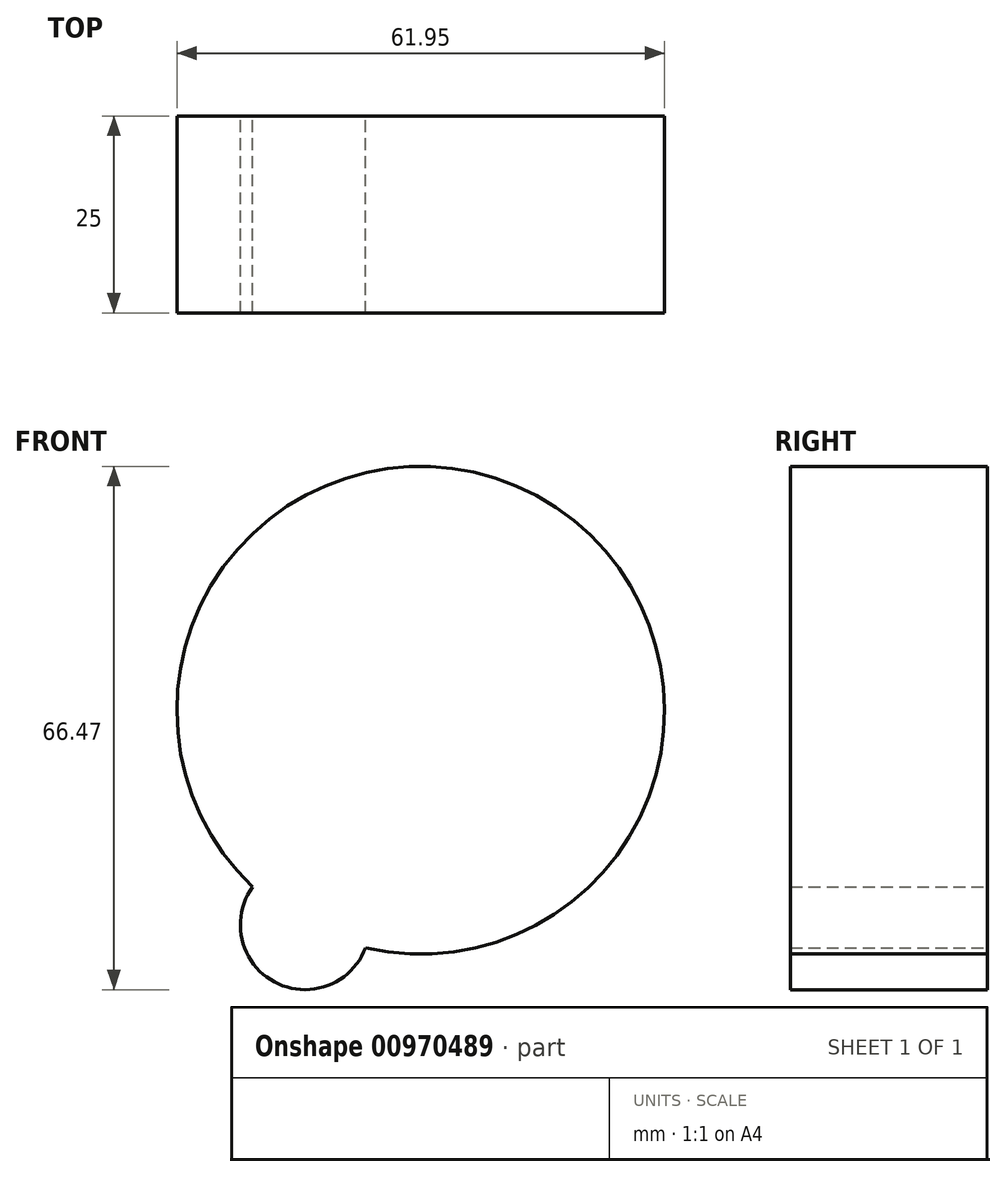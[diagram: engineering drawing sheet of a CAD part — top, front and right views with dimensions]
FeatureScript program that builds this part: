
annotation { "Feature Type Name" : "Feature", "Feature Type Description" : "" }
export const myFeature = defineFeature(function(context is Context, id is Id, definition is map)
    precondition{}
    {
        {
            var Q0;
            Q0=qCreatedBy(makeId("Front.planeOp"),FACE);
            var sketch = newSketch(context, id + "F0", { "sketchPlane" : qUnion([Q0])});
            skCircle(sketch, "E0", {"center": v(-116.66, 6.21) * mm, "radius": 30.97 * mm});
            skCircle(sketch, "E1", {"center": v(-131.35, -21.06) * mm, "radius": 8.22 * mm});
            skSolve(sketch);
        }
        {
            var Q0;
            Q0=qSketchRegion(id+"F0",true);
            extrude(context, id + "F1", {"entities" : qUnion([Q0]), "depth" : 25 * mm, "offsetDistance" : 25 * mm});
        }
    });
